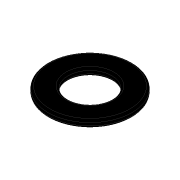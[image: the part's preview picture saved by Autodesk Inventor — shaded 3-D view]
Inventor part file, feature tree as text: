
AUTODESK INVENTOR PART (.ipt)
format: ipt  version: 2020 (Build 240168000, 168)  size: 122,880 bytes
history: native  units: mm
features: extrude x1, fillet x1, sketch x1
ambient origin geometry x8: Origin, YZ Plane, XZ Plane, XY Plane, X Axis, Y Axis, Z Axis, Center Point
bodies: Solid1 (feature_tree)
feature tree (3):
  extrude  "Extrusion1"  Depth=10.0mm
  fillet  "Fillet1"  Radius=0.85mm
  sketch  "Sketch1"  dims[d0=5.2mm d1=10.0mm d2=0.85mm d3=0.0mm d4=0.25mm]
